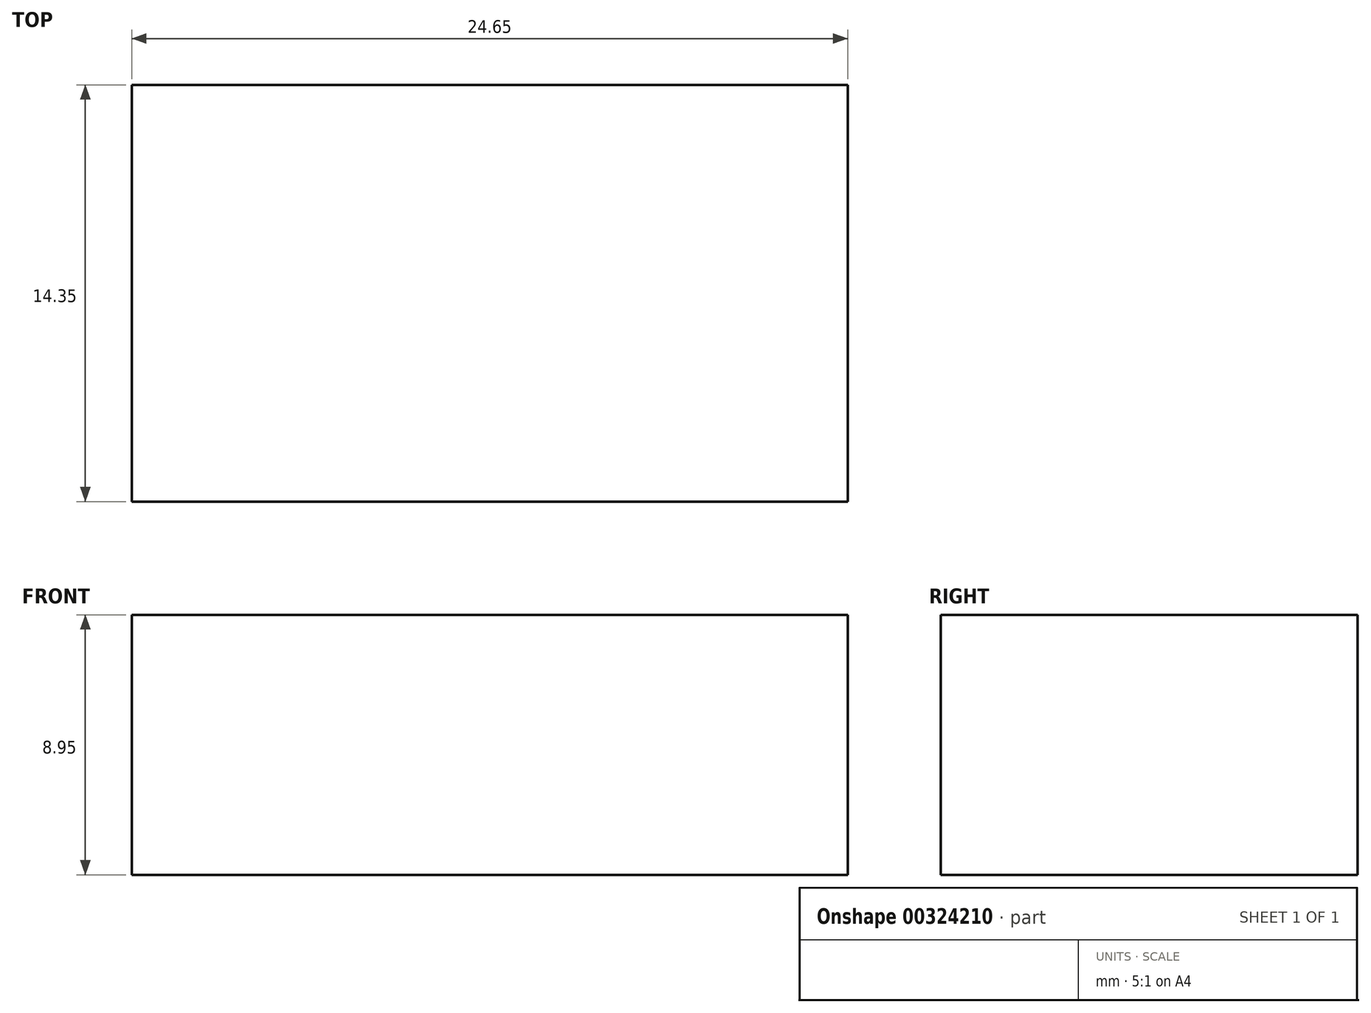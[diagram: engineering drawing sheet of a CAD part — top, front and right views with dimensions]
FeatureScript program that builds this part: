
annotation { "Feature Type Name" : "Feature", "Feature Type Description" : "" }
export const myFeature = defineFeature(function(context is Context, id is Id, definition is map)
    precondition{}
    {
        {
            var Q0;
            Q0=qCreatedBy(makeId("Front.planeOp"),FACE);
            var sketch = newSketch(context, id + "F0", { "sketchPlane" : qUnion([Q0])});
            skLineSegment(sketch, "E0.bottom", {"start": v(-24.65, 8.95) * mm, "end": v(0, 8.95) * mm});
            skLineSegment(sketch, "E0.top", {"start": v(-24.65, 0) * mm, "end": v(0, 0) * mm});
            skLineSegment(sketch, "E0.left", {"start": v(-24.65, 8.95) * mm, "end": v(-24.65, 0) * mm});
            skLineSegment(sketch, "E0.right", {"start": v(0, 8.95) * mm, "end": v(0, 0) * mm});
            skSolve(sketch);
        }
        {
            var Q0;
            Q0=makeQuery(id+"F0.imprint","IMPRINT",FACE,{"disambiguationData":[TD([[makeQuery(id+"F0.imprint","IMPRINT",EDGE,{"derivedFrom":sQuery(id+"F0.wireOp",EDGE,"E0.bottom")}),-1.0]])]});
            extrude(context, id + "F1", {"entities" : qUnion([Q0]), "depth" : 14.35 * mm});
        }
    });
